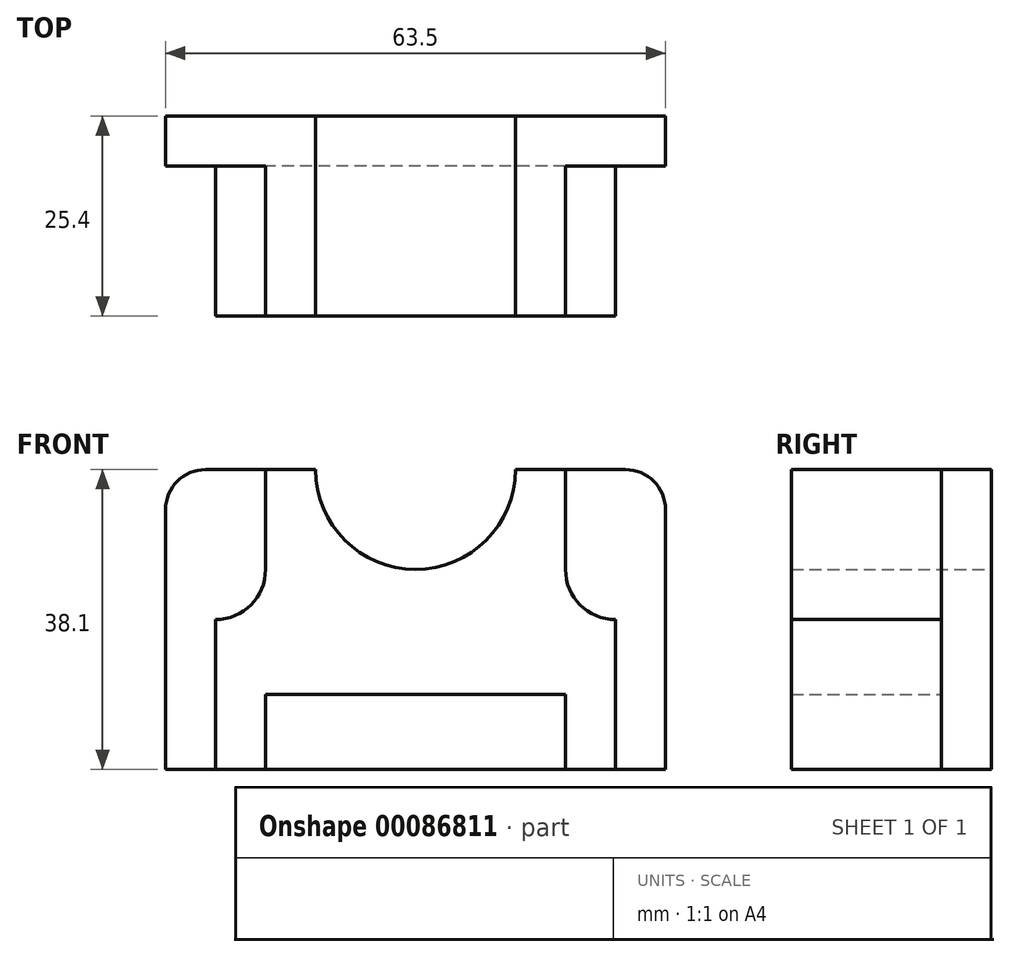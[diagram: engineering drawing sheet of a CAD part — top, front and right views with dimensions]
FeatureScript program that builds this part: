
annotation { "Feature Type Name" : "Feature", "Feature Type Description" : "" }
export const myFeature = defineFeature(function(context is Context, id is Id, definition is map)
    precondition{}
    {
        {
            var Q0;
            Q0=qCreatedBy(makeId("Front.planeOp"),FACE);
            var sketch = newSketch(context, id + "F0", { "sketchPlane" : qUnion([Q0])});
            skLineSegment(sketch, "E0", {"start": v(-44.45, 33.43) * mm, "end": v(19.05, 33.43) * mm});
            skLineSegment(sketch, "E1", {"start": v(19.05, 33.43) * mm, "end": v(19.05, -4.67) * mm});
            skLineSegment(sketch, "E2", {"start": v(19.05, -4.67) * mm, "end": v(-44.45, -4.67) * mm});
            skLineSegment(sketch, "E3", {"start": v(-44.45, 33.43) * mm, "end": v(-44.45, -4.67) * mm});
            skArc(sketch, "E4", {"start": v(-25.4, 33.43) * mm, "mid": v(-12.7, 20.73) * mm, "end": v(0, 33.43) * mm});
            skSolve(sketch);
        }
        {
            var Q0;
            Q0 = qSketchRegion(id + "F0", true);
            extrude(context, id + "F1", {"entities" : qUnion([Q0]), "depth" : 6.35 * mm});
        }
        {
            var Q0;
            Q0=makeQuery(id+"F1.opExtrude","SWEPT_EDGE",EDGE,{"disambiguationData":[OSD([sQuery(id+"F0.wireOp",EDGE,"E0"),sQuery(id+"F0.wireOp",EDGE,"E3")])]});
            var Q1;
            Q1=makeQuery(id+"F1.opExtrude","SWEPT_EDGE",EDGE,{"disambiguationData":[OSD([sQuery(id+"F0.wireOp",EDGE,"E0"),sQuery(id+"F0.wireOp",EDGE,"E1")])]});
            fillet(context, id + "F2", {"entities" : qUnion([Q0, Q1]), "radius" : 5.08 * mm, "tangentPropagation" : true, "allowEdgeOverflow" : false});
        }
        {
            var Q0;
            Q0=makeQuery(id+"F1.opExtrude","CAP_FACE",FACE,{"disambiguationData":[OSD([sQuery(id+"F0.wireOp",EDGE,"E0"),sQuery(id+"F0.wireOp",EDGE,"E1"),sQuery(id+"F0.wireOp",EDGE,"E2"),sQuery(id+"F0.wireOp",EDGE,"E3")])],"isStart":false});
            var sketch = newSketch(context, id + "F3", { "sketchPlane" : qUnion([Q0])});
            skLineSegment(sketch, "E5", {"start": v(-38.1, -4.67) * mm, "end": v(-38.1, 14.38) * mm});
            skLineSegment(sketch, "E6", {"start": v(-31.75, -4.67) * mm, "end": v(-31.75, 4.85) * mm});
            skPoint(sketch, "E6.endSnap0", {"position": v(-38.1, 4.85) * mm});
            skLineSegment(sketch, "E7", {"start": v(-31.75, 4.85) * mm, "end": v(6.35, 4.85) * mm});
            skLineSegment(sketch, "E8", {"start": v(6.35, 4.85) * mm, "end": v(6.35, -4.67) * mm});
            skLineSegment(sketch, "E9", {"start": v(12.7, -4.67) * mm, "end": v(12.7, 14.38) * mm});
            skLineSegment(sketch, "E10", {"start": v(-38.1, 14.38) * mm, "end": v(-38.1, 33.43) * mm});
            skLineSegment(sketch, "E11", {"start": v(12.7, 14.38) * mm, "end": v(12.7, 33.43) * mm});
            skLineSegment(sketch, "E12", {"start": v(-38.1, 33.43) * mm, "end": v(12.7, 33.43) * mm});
            skLineSegment(sketch, "E13", {"start": v(-38.1, -4.67) * mm, "end": v(-31.75, -4.67) * mm});
            skLineSegment(sketch, "E14", {"start": v(6.35, -4.67) * mm, "end": v(12.7, -4.67) * mm});
            skLineSegment(sketch, "E15", {"start": v(-38.1, 14.38) * mm, "end": v(-38.1, 14.38) * mm});
            skLineSegment(sketch, "E16", {"start": v(-31.75, 20.73) * mm, "end": v(-31.75, 33.43) * mm});
            skLineSegment(sketch, "E17", {"start": v(-31.75, 33.43) * mm, "end": v(-38.1, 33.43) * mm});
            skLineSegment(sketch, "E18", {"start": v(12.7, 14.38) * mm, "end": v(12.7, 14.38) * mm});
            skLineSegment(sketch, "E19", {"start": v(6.35, 20.73) * mm, "end": v(6.35, 33.43) * mm});
            skPoint(sketch, "E20.visualSharp", {"position": v(-31.75, 14.38) * mm});
            skArc(sketch, "E20.filletArc", {"start": v(-38.1, 14.38) * mm, "mid": v(-33.6, 16.24) * mm, "end": v(-31.75, 20.73) * mm});
            skPoint(sketch, "E21.visualSharp", {"position": v(6.35, 14.38) * mm});
            skArc(sketch, "E21.filletArc", {"start": v(6.35, 20.73) * mm, "mid": v(8.2, 16.24) * mm, "end": v(12.7, 14.38) * mm});
            skSolve(sketch);
        }
        {
            var Q0;
            Q0 = qSketchRegion(id + "F3", true);
            extrude(context, id + "F4", {"entities" : qUnion([Q0]), "operationType" : NewBodyOperationType.ADD, "depth" : 19.05 * mm});
        }
        {
            var Q0;
            {var subQ0=sQuery(id+"F0.wireOp",EDGE,"E4");Q0=makeQuery(id+"F0.imprint","IMPRINT",FACE,{"disambiguationData":[TD([[makeQuery(id+"F0.imprint","IMPRINT",EDGE,{"derivedFrom":subQ0}),1.0]])]});}
            extrude(context, id + "F5", {"entities" : qUnion([Q0]), "operationType" : NewBodyOperationType.REMOVE, "oppositeDirection" : true, "depth" : 25.4 * mm});
        }
        {
            var Q0;
            {var subQ0=sQuery(id+"F0.wireOp",EDGE,"E4");Q0=makeQuery(id+"F0.imprint","IMPRINT",FACE,{"disambiguationData":[TD([[makeQuery(id+"F0.imprint","IMPRINT",EDGE,{"derivedFrom":subQ0}),1.0]])]});}
            extrude(context, id + "F6", {"entities" : qUnion([Q0]), "operationType" : NewBodyOperationType.REMOVE, "depth" : 25.4 * mm});
        }
        {
            var Q0;
            Q0=makeQuery(id+"F3.imprint","IMPRINT",FACE,{"disambiguationData":[TD([[makeQuery(id+"F3.imprint","IMPRINT",EDGE,{"derivedFrom":sQuery(id+"F3.wireOp",EDGE,"E10")}),-1.0]])]});
            var Q1;
            Q1=makeQuery(id+"F4.opExtrude","CAP_FACE",FACE,{"disambiguationData":[OSD([sQuery(id+"F3.wireOp",EDGE,"E5"),sQuery(id+"F3.wireOp",EDGE,"E6"),sQuery(id+"F3.wireOp",EDGE,"E7"),sQuery(id+"F3.wireOp",EDGE,"E8"),sQuery(id+"F3.wireOp",EDGE,"E9"),sQuery(id+"F3.wireOp",EDGE,"E10"),sQuery(id+"F3.wireOp",EDGE,"E11"),sQuery(id+"F3.wireOp",EDGE,"E12"),sQuery(id+"F3.wireOp",EDGE,"E13"),sQuery(id+"F3.wireOp",EDGE,"E14"),sQuery(id+"F3.wireOp",EDGE,"E17")])],"isStart":false});
            extrude(context, id + "F7", {"entities" : qUnion([Q0, Q1]), "operationType" : NewBodyOperationType.REMOVE, "depth" : 72.56 * mm});
        }
        {
            var Q0;
            {var subQ0=sQuery(id+"F3.wireOp",EDGE,"E11");Q0=makeQuery(id+"F3.imprint","IMPRINT",FACE,{"disambiguationData":[TD([[makeQuery(id+"F3.imprint","IMPRINT",EDGE,{"derivedFrom":subQ0}),1.0]])]});}
            extrude(context, id + "F8", {"entities" : qUnion([Q0]), "operationType" : NewBodyOperationType.REMOVE, "depth" : 61.47 * mm});
        }
    });
